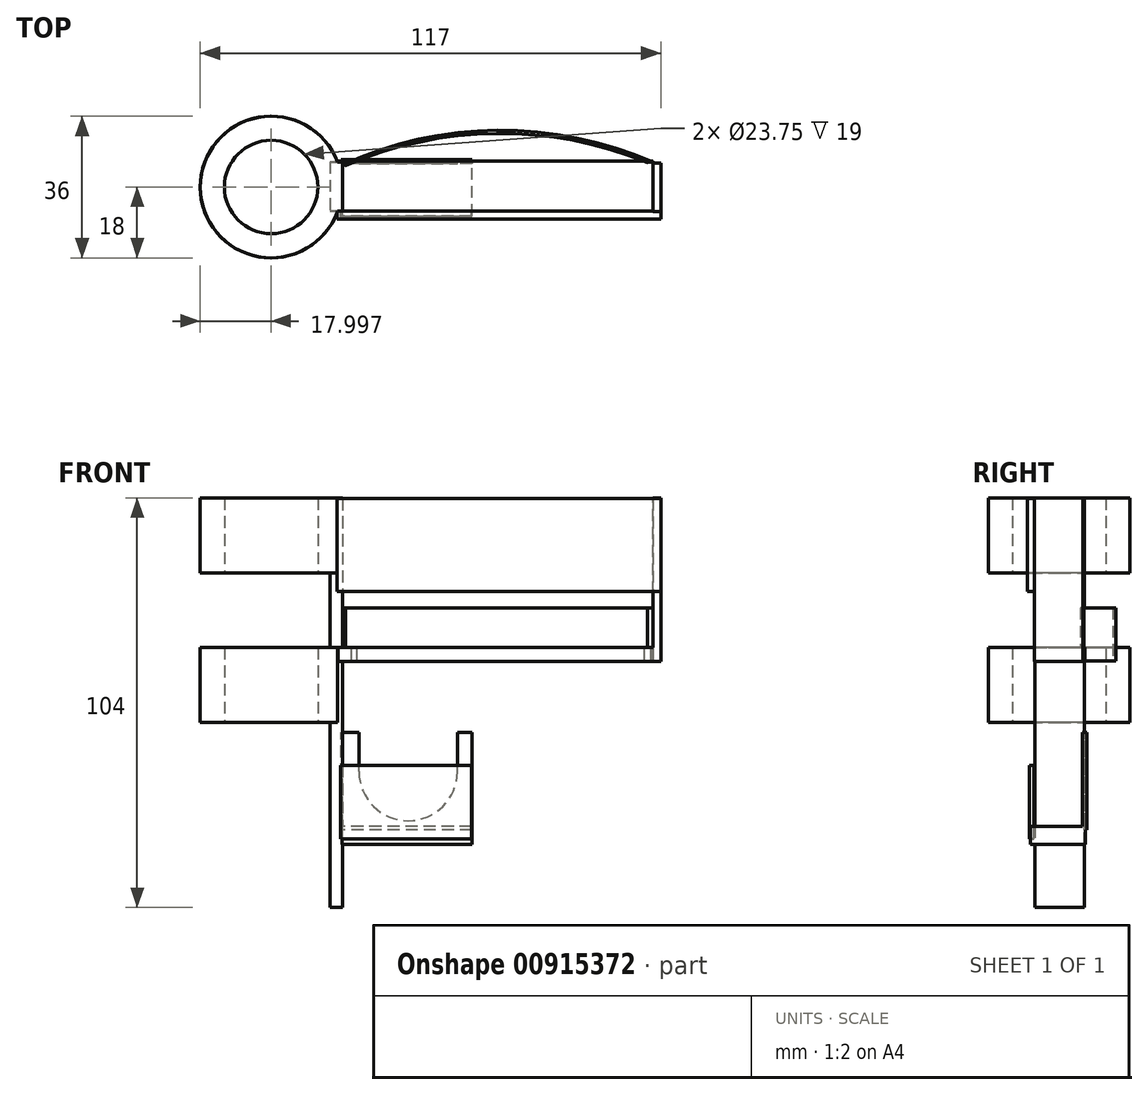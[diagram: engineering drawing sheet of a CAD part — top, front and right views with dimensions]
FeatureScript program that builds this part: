
annotation { "Feature Type Name" : "Feature", "Feature Type Description" : "" }
export const myFeature = defineFeature(function(context is Context, id is Id, definition is map)
    precondition{}
    {
        {
            var Q0;
            Q0=qCreatedBy(makeId("Top.planeOp"),FACE);
            var sketch = newSketch(context, id + "F0", { "sketchPlane" : qUnion([Q0])});
            skCircle(sketch, "E0", {"center": v(-64.56, 2.48) * mm, "radius": 18 * mm});
            skSolve(sketch);
        }
        {
            var Q0;
            Q0=qSketchRegion(id+"F0",true);
            extrude(context, id + "F1", {"entities" : qUnion([Q0]), "depth" : 8 * mm, "offsetDistance" : 25 * mm});
        }
        {
            var Q0;
            Q0=makeQuery(id+"F1.opExtrude","CAP_FACE",FACE,{"disambiguationData":[OSD([sQuery(id+"F0.wireOp",EDGE,"E0")])],"isStart":false});
            var sketch = newSketch(context, id + "F2", { "sketchPlane" : qUnion([Q0])});
            skCircle(sketch, "E1", {"center": v(-64.56, 2.48) * mm, "radius": 11.88 * mm});
            skSolve(sketch);
        }
        {
            var Q0;
            Q0=makeQuery(id+"F2.imprint","IMPRINT",FACE,{"disambiguationData":[TD([[makeQuery(id+"F2.imprint","IMPRINT",EDGE,{"derivedFrom":sQuery(id+"F2.wireOp",EDGE,"E1")}),-1.0]])]});
            extrude(context, id + "F3", {"entities" : qUnion([Q0]), "operationType" : NewBodyOperationType.ADD, "depth" : 96 * mm, "offsetDistance" : 25 * mm});
        }
        {
            var Q0;
            Q0=makeQuery(id+"F3.opExtrude","CAP_FACE",FACE,{"disambiguationData":[OSD([sQuery(id+"F0.wireOp",EDGE,"E0"),sQuery(id+"F2.wireOp",EDGE,"E1")])],"isStart":false});
            cPlane(context, id + "F4", {"entities" : qUnion([Q0]), "cplaneType" : CPlaneType.OFFSET, "offset" : 19 * mm, "oppositeDirection" : true, "width" : 150 * mm, "height" : 150 * mm});
        }
        {
            var Q0;
            Q0=qCreatedBy(id+"F4.planeOp",FACE);
            cPlane(context, id + "F5", {"entities" : qUnion([Q0]), "cplaneType" : CPlaneType.OFFSET, "offset" : 19 * mm, "oppositeDirection" : true, "width" : 150 * mm, "height" : 150 * mm});
        }
        {
            var Q0;
            Q0=qCreatedBy(id+"F5.planeOp",FACE);
            cPlane(context, id + "F6", {"entities" : qUnion([Q0]), "cplaneType" : CPlaneType.OFFSET, "offset" : 19 * mm, "oppositeDirection" : true, "width" : 150 * mm, "height" : 150 * mm});
        }
        {
            var Q0;
            Q0=qCreatedBy(id+"F5.planeOp",FACE);
            var sketch = newSketch(context, id + "F7", { "sketchPlane" : qUnion([Q0])});
            skLineSegment(sketch, "E2.bottom", {"start": v(-117.1, -27.67) * mm, "end": v(-2.84, -27.67) * mm});
            skLineSegment(sketch, "E2.top", {"start": v(-117.1, 43.37) * mm, "end": v(-2.84, 43.37) * mm});
            skLineSegment(sketch, "E2.left", {"start": v(-117.1, -27.67) * mm, "end": v(-117.1, 43.37) * mm});
            skLineSegment(sketch, "E2.right", {"start": v(-2.84, -27.67) * mm, "end": v(-2.84, 43.37) * mm});
            skSolve(sketch);
        }
        {
            var Q0;
            Q0=qSketchRegion(id+"F7",true);
            extrude(context, id + "F8", {"entities" : qUnion([Q0]), "operationType" : NewBodyOperationType.REMOVE, "depth" : 19 * mm, "offsetDistance" : 25 * mm});
        }
        {
            var Q0;
            Q0=qCreatedBy(id+"F6.planeOp",FACE);
            var sketch = newSketch(context, id + "F9", { "sketchPlane" : qUnion([Q0])});
            skLineSegment(sketch, "E3.bottom", {"start": v(-134.77, -40.96) * mm, "end": v(8.12, -40.96) * mm});
            skLineSegment(sketch, "E3.top", {"start": v(-134.77, 48.4) * mm, "end": v(8.12, 48.4) * mm});
            skLineSegment(sketch, "E3.left", {"start": v(-134.77, -40.96) * mm, "end": v(-134.77, 48.4) * mm});
            skLineSegment(sketch, "E3.right", {"start": v(8.12, -40.96) * mm, "end": v(8.12, 48.4) * mm});
            skSolve(sketch);
        }
        {
            var Q0;
            Q0=qSketchRegion(id+"F9",true);
            extrude(context, id + "F10", {"entities" : qUnion([Q0]), "operationType" : NewBodyOperationType.REMOVE, "oppositeDirection" : true, "depth" : 19 * mm, "offsetDistance" : 25 * mm});
        }
        {
            var Q0;
            Q0=qCreatedBy(makeId("Top.planeOp"),FACE);
            var sketch = newSketch(context, id + "F11", { "sketchPlane" : qUnion([Q0])});
            skLineSegment(sketch, "E4.bottom", {"start": v(-47.03, 8.87) * mm, "end": v(-50.03, 8.87) * mm});
            skLineSegment(sketch, "E4.top", {"start": v(-47.03, -3.63) * mm, "end": v(-50.03, -3.63) * mm});
            skLineSegment(sketch, "E5.bottom", {"start": v(-49.55, -3.63) * mm, "end": v(-46.43, -3.63) * mm});
            skLineSegment(sketch, "E5.top", {"start": v(-49.55, 8.87) * mm, "end": v(-46.43, 8.87) * mm});
            skLineSegment(sketch, "E5.left", {"start": v(-49.55, -3.63) * mm, "end": v(-49.55, 8.87) * mm});
            skLineSegment(sketch, "E5.right", {"start": v(-46.43, -3.63) * mm, "end": v(-46.43, 8.87) * mm});
            skSolve(sketch);
        }
        {
            var Q0;
            Q0=qSketchRegion(id+"F11",true);
            extrude(context, id + "F12", {"entities" : qUnion([Q0]), "depth" : 104 * mm, "offsetDistance" : 25 * mm});
        }
        {
            var Q0;
            Q0=makeQuery(id+"F3.opExtrude","CAP_FACE",FACE,{"disambiguationData":[OSD([sQuery(id+"F0.wireOp",EDGE,"E0"),sQuery(id+"F2.wireOp",EDGE,"E1")])],"isStart":false});
            cPlane(context, id + "F13", {"entities" : qUnion([Q0]), "cplaneType" : CPlaneType.OFFSET, "offset" : 38 * mm, "oppositeDirection" : true, "width" : 150 * mm, "height" : 150 * mm});
        }
        {
            var Q0;
            Q0=qCreatedBy(id+"F13.planeOp",FACE);
            var sketch = newSketch(context, id + "F14", { "sketchPlane" : qUnion([Q0])});
            skLineSegment(sketch, "E6.bottom", {"start": v(-47.56, -3.77) * mm, "end": v(32.44, -3.77) * mm});
            skLineSegment(sketch, "E6.top", {"start": v(-47.56, 9.06) * mm, "end": v(32.44, 9.06) * mm});
            skLineSegment(sketch, "E6.left", {"start": v(-47.56, -3.77) * mm, "end": v(-47.56, 9.06) * mm});
            skLineSegment(sketch, "E6.right", {"start": v(32.44, -3.77) * mm, "end": v(32.44, 9.06) * mm});
            skSolve(sketch);
        }
        {
            var Q0;
            Q0=qSketchRegion(id+"F14",true);
            extrude(context, id + "F15", {"entities" : qUnion([Q0]), "operationType" : NewBodyOperationType.ADD, "oppositeDirection" : true, "depth" : 3.5 * mm, "offsetDistance" : 25 * mm});
        }
        {
            var Q0;
            Q0=makeQuery(id+"F15.opExtrude","SWEPT_FACE",FACE,{"disambiguationData":[OSD([sQuery(id+"F14.wireOp",EDGE,"E6.right")])]});
            var sketch = newSketch(context, id + "F16", { "sketchPlane" : qUnion([Q0])});
            skLineSegment(sketch, "E7.bottom", {"start": v(-3.77, 62.5) * mm, "end": v(8.53, 62.5) * mm});
            skLineSegment(sketch, "E7.top", {"start": v(-3.77, 104) * mm, "end": v(8.53, 104) * mm});
            skLineSegment(sketch, "E7.left", {"start": v(-3.77, 62.5) * mm, "end": v(-3.77, 104) * mm});
            skLineSegment(sketch, "E7.right", {"start": v(8.53, 62.5) * mm, "end": v(8.53, 104) * mm});
            skSolve(sketch);
        }
        {
            var Q0;
            {var subQ0=sQuery(id+"F16.wireOp",EDGE,"E7.top");Q0=makeQuery(id+"F16.imprint","IMPRINT",FACE,{"disambiguationData":[TD([[makeQuery(id+"F16.imprint","IMPRINT",EDGE,{"derivedFrom":subQ0}),-1.0]])]});}
            var Q1;
            {var subQ0=sQuery(id+"F16.wireOp",EDGE,"E7.bottom");Q1=makeQuery(id+"F16.imprint","IMPRINT",FACE,{"disambiguationData":[TD([[makeQuery(id+"F16.imprint","IMPRINT",EDGE,{"derivedFrom":subQ0}),1.0]])]});}
            extrude(context, id + "F17", {"entities" : qUnion([Q0, Q1]), "operationType" : NewBodyOperationType.ADD, "depth" : 2 * mm, "offsetDistance" : 25 * mm});
        }
        {
            var Q0;
            Q0=makeQuery(id+"F12.opExtrude","SWEPT_FACE",FACE,{"disambiguationData":[OSD([sQuery(id+"F11.wireOp",EDGE,"E5.bottom")])]});
            var sketch = newSketch(context, id + "F18", { "sketchPlane" : qUnion([Q0])});
            skLineSegment(sketch, "E8.bottom", {"start": v(-47.77, 80.27) * mm, "end": v(34.43, 80.27) * mm});
            skLineSegment(sketch, "E8.top", {"start": v(-47.77, 103.88) * mm, "end": v(34.43, 103.88) * mm});
            skLineSegment(sketch, "E8.left", {"start": v(-47.77, 80.27) * mm, "end": v(-47.77, 103.88) * mm});
            skLineSegment(sketch, "E8.right", {"start": v(34.43, 80.27) * mm, "end": v(34.43, 103.88) * mm});
            skSolve(sketch);
        }
        {
            var Q0;
            Q0=qSketchRegion(id+"F18",true);
            extrude(context, id + "F19", {"entities" : qUnion([Q0]), "operationType" : NewBodyOperationType.ADD, "depth" : 2 * mm, "offsetDistance" : 25 * mm});
        }
        {
            var Q0;
            Q0=qCreatedBy(makeId("Top.planeOp"),FACE);
            cPlane(context, id + "F20", {"entities" : qUnion([Q0]), "cplaneType" : CPlaneType.OFFSET, "offset" : 62.6 * mm, "width" : 150 * mm, "height" : 150 * mm});
        }
        {
            var Q0;
            Q0=qCreatedBy(id+"F20.planeOp",FACE);
            var sketch = newSketch(context, id + "F21", { "sketchPlane" : qUnion([Q0])});
            skArc(sketch, "E9", {"start": v(32.5, 8.77) * mm, "mid": v(-7.15, 16.88) * mm, "end": v(-46.63, 8.01) * mm});
            skArc(sketch, "E10", {"start": v(31.06, 8.73) * mm, "mid": v(-7.35, 16.1) * mm, "end": v(-45.6, 7.94) * mm});
            skLineSegment(sketch, "E11", {"start": v(-46.63, 8.01) * mm, "end": v(-45.6, 7.94) * mm});
            skLineSegment(sketch, "E12", {"start": v(31.06, 8.73) * mm, "end": v(32.5, 8.77) * mm});
            skLineSegment(sketch, "E13", {"start": v(32.5, 8.77) * mm, "end": v(34.01, 8.1) * mm});
            skLineSegment(sketch, "E14", {"start": v(34.01, 8.1) * mm, "end": v(34.01, 7.49) * mm});
            skLineSegment(sketch, "E15", {"start": v(34.01, 7.49) * mm, "end": v(33.25, 7.49) * mm});
            skLineSegment(sketch, "E16", {"start": v(33.25, 7.49) * mm, "end": v(32.5, 8.23) * mm});
            skLineSegment(sketch, "E17", {"start": v(32.5, 8.23) * mm, "end": v(31.06, 8.73) * mm});
            skSolve(sketch);
        }
        {
            var Q0;
            Q0=makeQuery(id+"F21.imprint","IMPRINT",FACE,{"disambiguationData":[TD([[makeQuery(id+"F21.imprint","IMPRINT",EDGE,{"derivedFrom":sQuery(id+"F21.wireOp",EDGE,"E9")}),1.0]])]});
            extrude(context, id + "F22", {"entities" : qUnion([Q0]), "operationType" : NewBodyOperationType.ADD, "depth" : 13.5 * mm, "offsetDistance" : 25 * mm});
        }
        {
            var Q0;
            Q0=qCreatedBy(makeId("Front.planeOp"),FACE);
            cPlane(context, id + "F23", {"entities" : qUnion([Q0]), "cplaneType" : CPlaneType.OFFSET, "offset" : 3.9 * mm, "width" : 150 * mm, "height" : 150 * mm});
        }
        {
            var Q0;
            Q0=qCreatedBy(makeId("Front.planeOp"),FACE);
            cPlane(context, id + "F24", {"entities" : qUnion([Q0]), "cplaneType" : CPlaneType.OFFSET, "offset" : 9.5 * mm, "oppositeDirection" : true, "width" : 150 * mm, "height" : 150 * mm});
        }
        {
            var Q0;
            Q0=makeQuery(id+"F10.boolean.opBoolean","SPLIT",BODY,{"disambiguationData":[OD(1.0)],"derivedFrom":makeQuery(id+"F8.boolean.opBoolean","SPLIT",BODY,{"disambiguationData":[OD(0.0)],"derivedFrom":makeQuery(id+"F1.opExtrude","SWEPT_BODY",BODY,{"disambiguationData":[OSD([sQuery(id+"F0.wireOp",EDGE,"E0")])]})})});
            deleteBodies(context, id + "F25", {"entities" : qUnion([Q0])});
        }
        {
            var Q0;
            Q0=makeQuery(id+"F17.boolean.opBoolean","MERGE",FACE,{"derivedFrom":[makeQuery(id+"F15.opExtrude","CAP_FACE",FACE,{"disambiguationData":[OSD([sQuery(id+"F14.wireOp",EDGE,"E6.bottom"),sQuery(id+"F14.wireOp",EDGE,"E6.top"),sQuery(id+"F14.wireOp",EDGE,"E6.left"),sQuery(id+"F14.wireOp",EDGE,"E6.right")])],"isStart":false}),makeQuery(id+"F17.opExtrude","SWEPT_FACE",FACE,{"disambiguationData":[OSD([sQuery(id+"F16.wireOp",EDGE,"E7.bottom")])]})]});
            cPlane(context, id + "F26", {"entities" : qUnion([Q0]), "cplaneType" : CPlaneType.OFFSET, "offset" : 46.5 * mm, "width" : 150 * mm, "height" : 150 * mm});
        }
        {
            var Q0;
            Q0=qCreatedBy(id+"F26.planeOp",FACE);
            var sketch = newSketch(context, id + "F27", { "sketchPlane" : qUnion([Q0])});
            skLineSegment(sketch, "E18.bottom", {"start": v(-46.54, 4.84) * mm, "end": v(-13.54, 4.84) * mm});
            skLineSegment(sketch, "E18.top", {"start": v(-46.54, -9.16) * mm, "end": v(-13.54, -9.16) * mm});
            skLineSegment(sketch, "E18.left", {"start": v(-46.54, 4.84) * mm, "end": v(-46.54, -9.16) * mm});
            skLineSegment(sketch, "E18.right", {"start": v(-13.54, 4.84) * mm, "end": v(-13.54, -9.16) * mm});
            skSolve(sketch);
        }
        {
            var Q0;
            Q0 = qSketchRegion(id + "F27", true);
            extrude(context, id + "F28", {"entities" : qUnion([Q0]), "operationType" : NewBodyOperationType.ADD, "oppositeDirection" : true, "depth" : 4.6 * mm, "offsetDistance" : 25 * mm});
        }
        {
            var Q0;
            Q0=qCreatedBy(id+"F24.planeOp",FACE);
            var sketch = newSketch(context, id + "F29", { "sketchPlane" : qUnion([Q0])});
            skLineSegment(sketch, "E19.bottom", {"start": v(-13.53, 19.7) * mm, "end": v(-46.84, 19.7) * mm});
            skLineSegment(sketch, "E19.top", {"start": v(-13.53, 44.49) * mm, "end": v(-46.84, 44.49) * mm});
            skLineSegment(sketch, "E19.left", {"start": v(-13.53, 19.7) * mm, "end": v(-13.53, 44.49) * mm});
            skLineSegment(sketch, "E19.right", {"start": v(-46.84, 19.7) * mm, "end": v(-46.84, 44.49) * mm});
            skCircle(sketch, "E20", {"center": v(-29.75, 34.47) * mm, "radius": 12.5 * mm});
            skLineSegment(sketch, "E21", {"start": v(-17.25, 34.47) * mm, "end": v(-17.25, 44.49) * mm});
            skLineSegment(sketch, "E22", {"start": v(-42.25, 34.47) * mm, "end": v(-42.25, 44.49) * mm});
            skSolve(sketch);
        }
        {
            var Q0;
            Q0=makeQuery(id+"F29.imprint","IMPRINT",FACE,{"disambiguationData":[TD([[makeQuery(id+"F29.imprint","IMPRINT",EDGE,{"derivedFrom":sQuery(id+"F29.wireOp",EDGE,"E19.bottom")}),-1.0]])]});
            extrude(context, id + "F30", {"entities" : qUnion([Q0]), "operationType" : NewBodyOperationType.ADD, "depth" : 1.1 * mm, "offsetDistance" : 25 * mm});
        }
        {
            var Q0;
            Q0=qCreatedBy(id+"F23.planeOp",FACE);
            var sketch = newSketch(context, id + "F31", { "sketchPlane" : qUnion([Q0])});
            skLineSegment(sketch, "E23.bottom", {"start": v(-13.64, 17.36) * mm, "end": v(-46.91, 17.36) * mm});
            skLineSegment(sketch, "E23.top", {"start": v(-13.64, 36.04) * mm, "end": v(-46.91, 36.04) * mm});
            skLineSegment(sketch, "E23.left", {"start": v(-13.64, 17.36) * mm, "end": v(-13.64, 36.04) * mm});
            skLineSegment(sketch, "E23.right", {"start": v(-46.91, 17.36) * mm, "end": v(-46.91, 36.04) * mm});
            skSolve(sketch);
        }
        {
            var Q0;
            Q0 = qSketchRegion(id + "F31", true);
            extrude(context, id + "F32", {"entities" : qUnion([Q0]), "operationType" : NewBodyOperationType.ADD, "depth" : 1.2 * mm, "offsetDistance" : 25 * mm});
        }
    });
